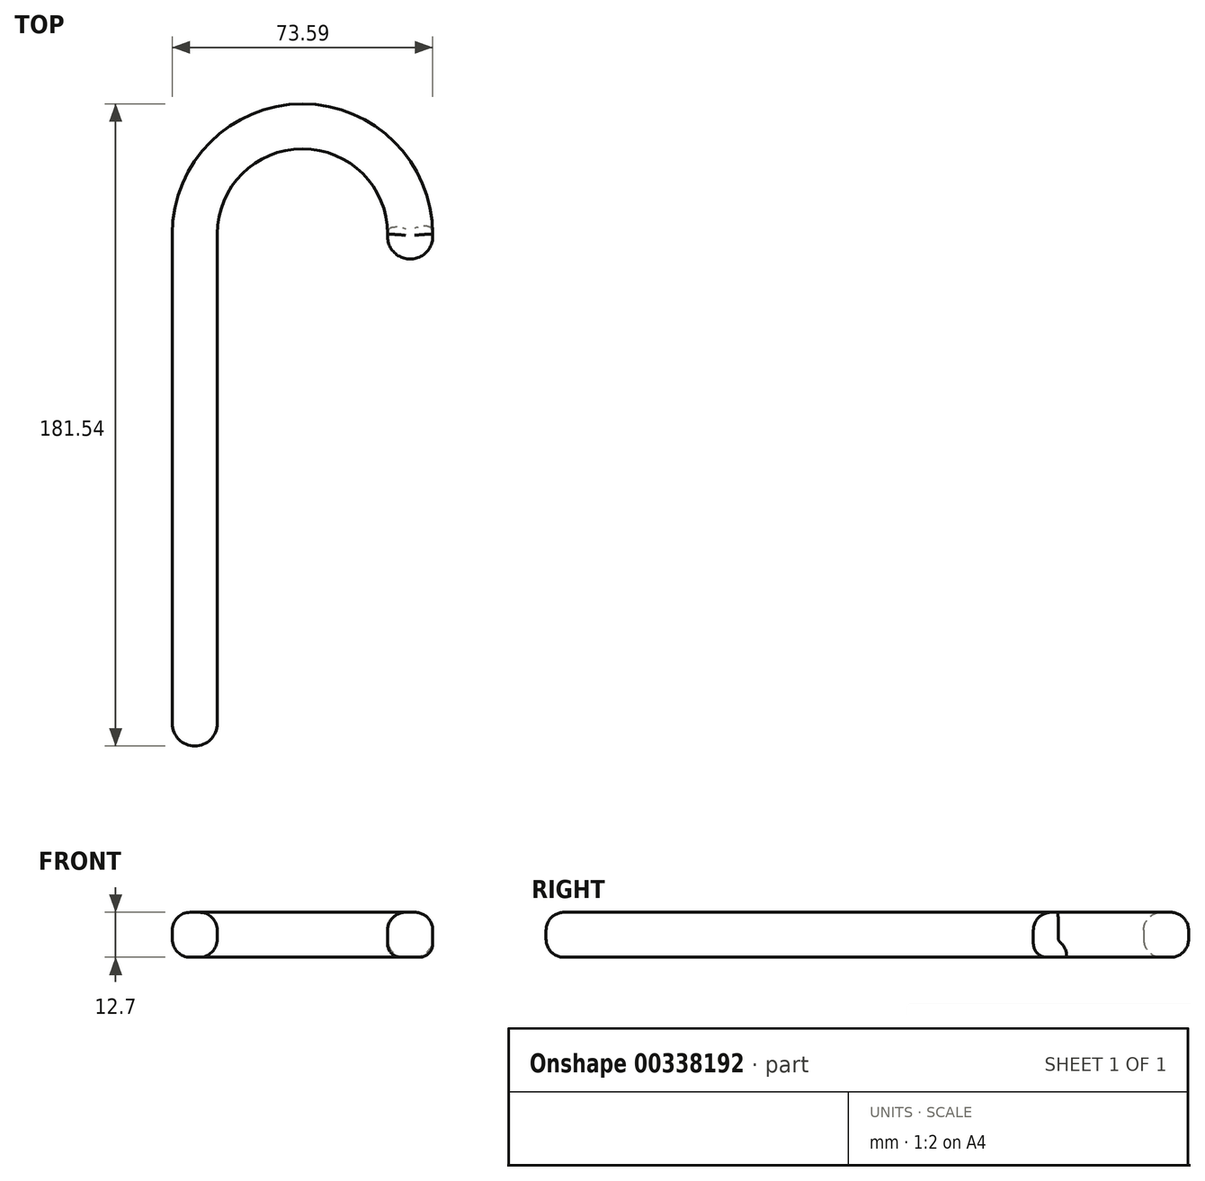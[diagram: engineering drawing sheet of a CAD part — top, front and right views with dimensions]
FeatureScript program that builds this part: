
annotation { "Feature Type Name" : "Feature", "Feature Type Description" : "" }
export const myFeature = defineFeature(function(context is Context, id is Id, definition is map)
    precondition{}
    {
        {
            var Q0;
            Q0=qCreatedBy(makeId("Top.planeOp"),FACE);
            var sketch = newSketch(context, id + "F0", { "sketchPlane" : qUnion([Q0])});
            skArc(sketch, "E0", {"start": v(0, 0) * mm, "mid": v(-36.78, 36.78) * mm, "end": v(-73.55, 0) * mm});
            skLineSegment(sketch, "E1", {"start": v(-73.55, 0) * mm, "end": v(-73.55, -138.41) * mm});
            skArc(sketch, "E2", {"start": v(-73.55, -138.41) * mm, "mid": v(-67.2, -144.76) * mm, "end": v(-60.85, -138.41) * mm});
            skLineSegment(sketch, "E3.0", {"start": v(-60.85, 0) * mm, "end": v(-60.85, -138.41) * mm});
            skArc(sketch, "E4.0", {"start": v(-12.7, 0) * mm, "mid": v(-36.78, 24.08) * mm, "end": v(-60.85, 0) * mm});
            skArc(sketch, "E5", {"start": v(-12.7, 0) * mm, "mid": v(-6.35, -7.1) * mm, "end": v(0, 0) * mm});
            skSolve(sketch);
        }
        {
            var Q0;
            Q0 = qSketchRegion(id + "F0", true);
            extrude(context, id + "F1", {"entities" : qUnion([Q0]), "depth" : 12.7 * mm});
        }
        {
            var Q0;
            Q0=makeQuery(id+"F1.opExtrude","CAP_FACE",FACE,{"disambiguationData":[OSD([sQuery(id+"F0.wireOp",EDGE,"E0"),sQuery(id+"F0.wireOp",EDGE,"E1"),sQuery(id+"F0.wireOp",EDGE,"E2"),sQuery(id+"F0.wireOp",EDGE,"E3.0"),sQuery(id+"F0.wireOp",EDGE,"E4.0"),sQuery(id+"F0.wireOp",EDGE,"E5")])],"isStart":false});
            fillet(context, id + "F2", {"entities" : qUnion([Q0]), "radius" : 5.08 * mm, "tangentPropagation" : true, "allowEdgeOverflow" : false});
        }
        {
            var Q0;
            Q0=makeQuery(id+"F1.opExtrude","CAP_EDGE",EDGE,{"disambiguationData":[OSD([sQuery(id+"F0.wireOp",EDGE,"E1")])],"isStart":true});
            fillet(context, id + "F3", {"entities" : qUnion([Q0]), "radius" : 5.08 * mm, "tangentPropagation" : true, "allowEdgeOverflow" : false});
        }
        {
            var Q0;
            Q0=makeQuery(id+"F1.opExtrude","CAP_EDGE",EDGE,{"disambiguationData":[OSD([sQuery(id+"F0.wireOp",EDGE,"E5")])],"isStart":true});
            fillet(context, id + "F4", {"entities" : qUnion([Q0]), "radius" : 3.8 * mm, "tangentPropagation" : true, "allowEdgeOverflow" : false});
        }
    });
